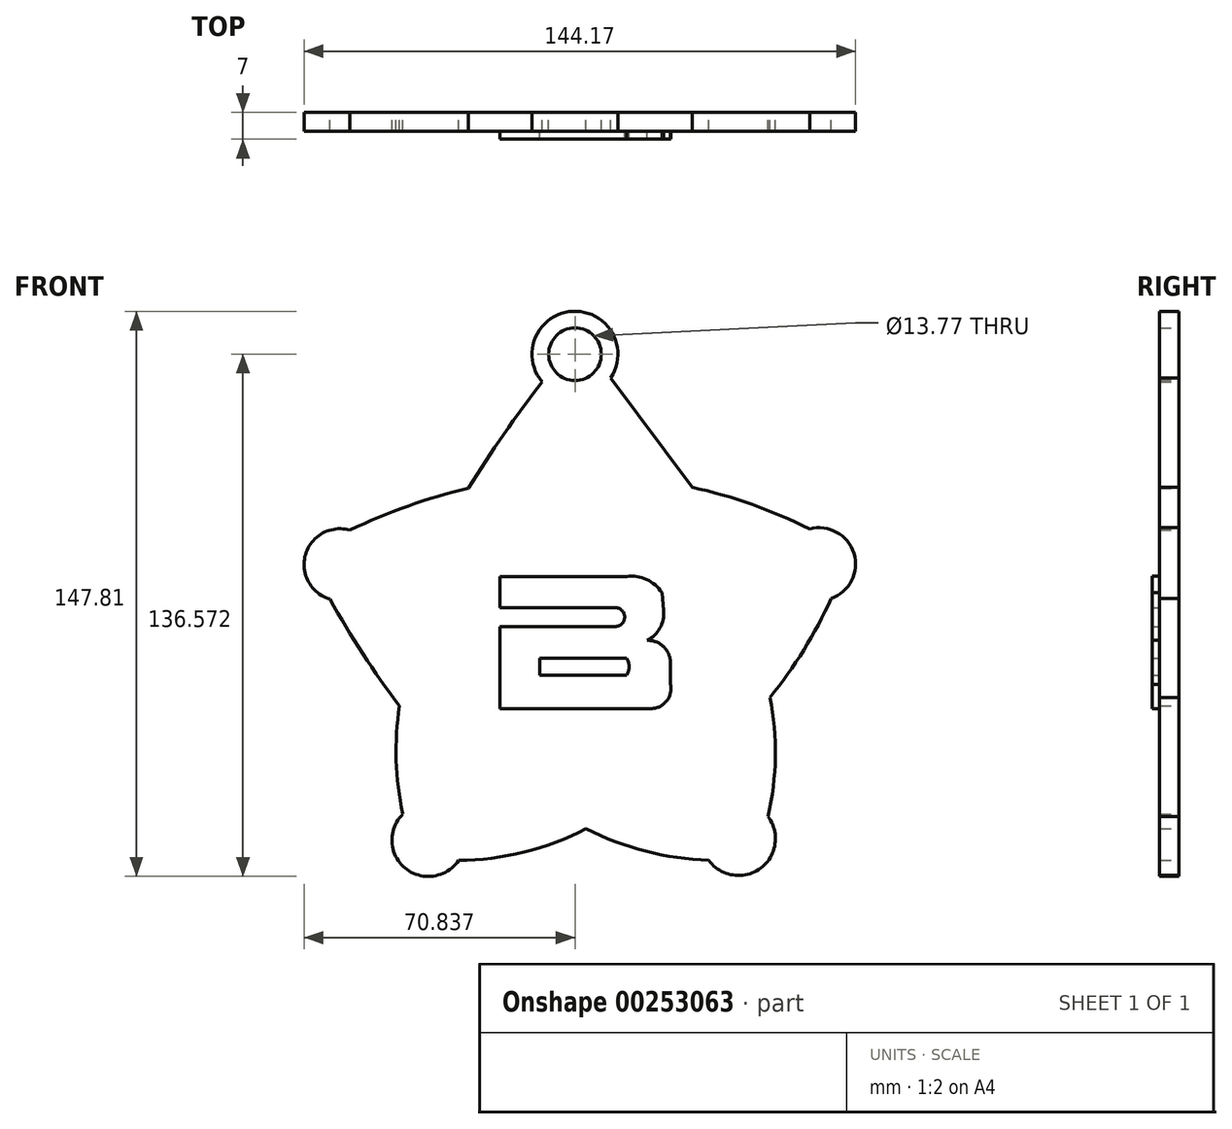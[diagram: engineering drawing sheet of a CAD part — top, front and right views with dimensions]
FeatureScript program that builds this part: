
annotation { "Feature Type Name" : "Feature", "Feature Type Description" : "" }
export const myFeature = defineFeature(function(context is Context, id is Id, definition is map)
    precondition{}
    {
        {
            var Q0;
            Q0=qCreatedBy(makeId("Front.planeOp"),FACE);
            var sketch = newSketch(context, id + "F0", { "sketchPlane" : qUnion([Q0])});
            skArc(sketch, "E0", {"start": v(11.25, 56.17) * mm, "mid": v(1.25, 73.58) * mm, "end": v(-6.75, 55.16) * mm});
            skArc(sketch, "E1", {"start": v(-6.75, 55.16) * mm, "mid": v(-16.71, 41.46) * mm, "end": v(-26.03, 27.31) * mm});
            skArc(sketch, "E2", {"start": v(-26.03, 27.31) * mm, "mid": v(-41.78, 22.64) * mm, "end": v(-56.96, 16.34) * mm});
            skArc(sketch, "E3", {"start": v(-56.96, 16.34) * mm, "mid": v(-68.6, 9.93) * mm, "end": v(-62.15, -1.69) * mm});
            skArc(sketch, "E4", {"start": v(-62.15, -1.69) * mm, "mid": v(-53.6, -15.99) * mm, "end": v(-44.03, -29.61) * mm});
            skArc(sketch, "E5", {"start": v(-44.03, -29.61) * mm, "mid": v(-44.87, -43.8) * mm, "end": v(-43.12, -57.9) * mm});
            skArc(sketch, "E6", {"start": v(-43.12, -57.9) * mm, "mid": v(-42.57, -72) * mm, "end": v(-28.58, -70) * mm});
            skArc(sketch, "E7", {"start": v(-28.58, -70) * mm, "mid": v(-11.4, -67.84) * mm, "end": v(4.78, -61.7) * mm});
            skArc(sketch, "E8", {"start": v(4.78, -61.7) * mm, "mid": v(20.37, -67.61) * mm, "end": v(36.88, -70) * mm});
            skArc(sketch, "E9", {"start": v(36.88, -70) * mm, "mid": v(50.4, -72.05) * mm, "end": v(52.32, -58.5) * mm});
            skArc(sketch, "E10", {"start": v(52.32, -58.5) * mm, "mid": v(54.27, -42.96) * mm, "end": v(52.86, -27.37) * mm});
            skArc(sketch, "E11", {"start": v(52.86, -27.37) * mm, "mid": v(61.7, -14.97) * mm, "end": v(68.85, -1.52) * mm});
            skArc(sketch, "E12", {"start": v(68.85, -1.52) * mm, "mid": v(74.79, 10.28) * mm, "end": v(63.22, 16.65) * mm});
            skArc(sketch, "E13", {"start": v(63.22, 16.65) * mm, "mid": v(48.21, 23.07) * mm, "end": v(32.52, 27.55) * mm});
            skLineSegment(sketch, "E14", {"start": v(11.25, 56.17) * mm, "end": v(32.52, 27.55) * mm});
            skCircle(sketch, "E15", {"center": v(1.88, 62.36) * mm, "radius": 6.89 * mm});
            skSolve(sketch);
        }
        {
            var Q0;
            Q0=makeQuery(id+"F0.imprint","IMPRINT",FACE,{"disambiguationData":[TD([[makeQuery(id+"F0.imprint","IMPRINT",EDGE,{"derivedFrom":sQuery(id+"F0.wireOp",EDGE,"E0")}),1.0]])]});
            var sketch = newSketch(context, id + "F1", { "sketchPlane" : qUnion([Q0])});
            skLineSegment(sketch, "E16", {"start": v(-17.72, 4.18) * mm, "end": v(-17.72, -3.92) * mm});
            skLineSegment(sketch, "E17", {"start": v(-17.72, -3.92) * mm, "end": v(12.4, -3.92) * mm});
            skArc(sketch, "E18", {"start": v(12.4, -8.87) * mm, "mid": v(14.87, -6.4) * mm, "end": v(12.4, -3.92) * mm});
            skLineSegment(sketch, "E19", {"start": v(12.4, -8.87) * mm, "end": v(-17.78, -8.87) * mm});
            skLineSegment(sketch, "E20", {"start": v(-17.78, -8.87) * mm, "end": v(-17.72, -30.4) * mm});
            skLineSegment(sketch, "E21", {"start": v(-17.72, -30.4) * mm, "end": v(21.75, -30.3) * mm});
            skArc(sketch, "E22", {"start": v(21.75, -30.3) * mm, "mid": v(25.8, -28.36) * mm, "end": v(26.85, -23.99) * mm});
            skLineSegment(sketch, "E23", {"start": v(26.85, -23.99) * mm, "end": v(26.85, -18.39) * mm});
            skArc(sketch, "E24", {"start": v(26.85, -18.39) * mm, "mid": v(25.05, -14.14) * mm, "end": v(20.74, -12.48) * mm});
            skArc(sketch, "E25", {"start": v(20.74, -12.48) * mm, "mid": v(24.1, -9.27) * mm, "end": v(25.05, -4.72) * mm});
            skPoint(sketch, "E25.endSnap0", {"position": v(25.05, -14.14) * mm});
            skLineSegment(sketch, "E26", {"start": v(25.05, -4.72) * mm, "end": v(24.6, 0) * mm});
            skArc(sketch, "E27", {"start": v(24.6, 0) * mm, "mid": v(20.6, 3.48) * mm, "end": v(15.33, 4.22) * mm});
            skLineSegment(sketch, "E28", {"start": v(15.33, 4.22) * mm, "end": v(-17.72, 4.18) * mm});
            skLineSegment(sketch, "E29", {"start": v(-7.33, -17.19) * mm, "end": v(-7.33, -21.56) * mm});
            skLineSegment(sketch, "E30", {"start": v(-7.33, -21.56) * mm, "end": v(15.33, -21.53) * mm});
            skArc(sketch, "E31", {"start": v(15.33, -21.53) * mm, "mid": v(16.01, -19.36) * mm, "end": v(15.33, -17.19) * mm});
            skLineSegment(sketch, "E32", {"start": v(-7.33, -17.19) * mm, "end": v(15.33, -17.19) * mm});
            skSolve(sketch);
        }
        {
            var Q0;
            Q0=makeQuery(id+"F0.imprint","IMPRINT",FACE,{"disambiguationData":[TD([[makeQuery(id+"F0.imprint","IMPRINT",EDGE,{"derivedFrom":sQuery(id+"F0.wireOp",EDGE,"E0")}),1.0]])]});
            extrude(context, id + "F2", {"entities" : qUnion([Q0]), "depth" : 5 * mm, "offsetDistance" : 25 * mm});
        }
        {
            var Q0;
            Q0 = qSketchRegion(id + "F1", true);
            extrude(context, id + "F3", {"entities" : qUnion([Q0]), "operationType" : NewBodyOperationType.ADD, "depth" : 7 * mm, "offsetDistance" : 25 * mm});
        }
    });
